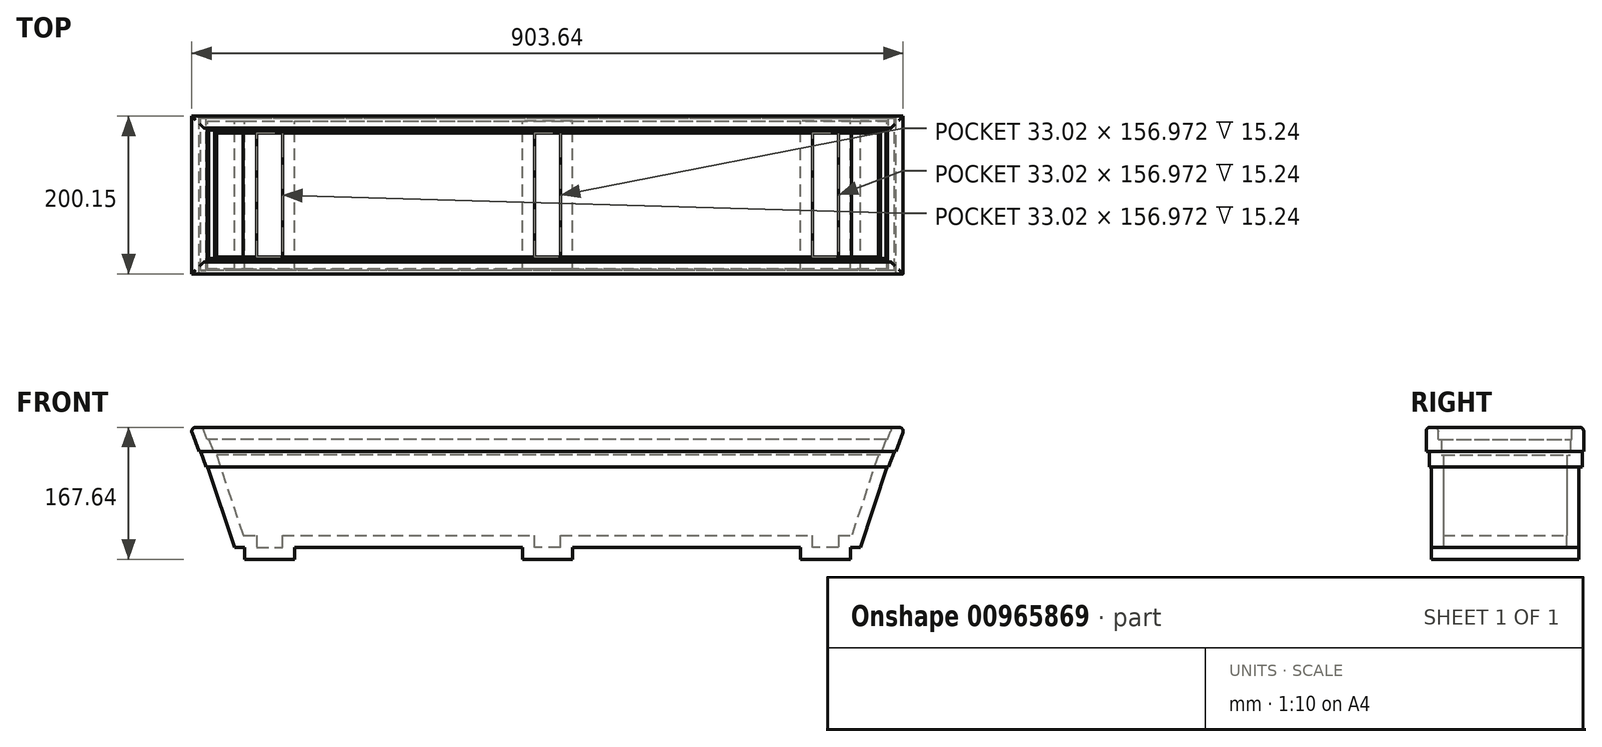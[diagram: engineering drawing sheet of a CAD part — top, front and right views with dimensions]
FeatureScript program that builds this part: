
annotation { "Feature Type Name" : "Feature", "Feature Type Description" : "" }
export const myFeature = defineFeature(function(context is Context, id is Id, definition is map)
    precondition{}
    {
        {
            var Q0;
            Q0=qCreatedBy(makeId("Front.planeOp"),FACE);
            var sketch = newSketch(context, id + "F0", { "sketchPlane" : qUnion([Q0])});
            skLineSegment(sketch, "E0", {"start": v(-96.9, 71.44) * mm, "end": v(811.15, 71.44) * mm});
            skLineSegment(sketch, "E1", {"start": v(-85.58, 40.7) * mm, "end": v(-83.56, 40.7) * mm});
            skLineSegment(sketch, "E2", {"start": v(-83.56, 40.7) * mm, "end": v(-76.36, 21.22) * mm});
            skLineSegment(sketch, "E3", {"start": v(-74.34, 21.22) * mm, "end": v(-40.27, -80.96) * mm});
            skLineSegment(sketch, "E4", {"start": v(-85.58, 40.7) * mm, "end": v(-96.9, 71.44) * mm});
            skLineSegment(sketch, "E5", {"start": v(-74.34, 21.22) * mm, "end": v(-76.36, 21.22) * mm});
            skLineSegment(sketch, "E6", {"start": v(-40.27, -80.96) * mm, "end": v(754.52, -80.96) * mm});
            skLineSegment(sketch, "E7.MirrorCS", {"start": v(799.83, 40.7) * mm, "end": v(797.8, 40.7) * mm});
            skLineSegment(sketch, "E8.MirrorCS", {"start": v(799.83, 40.7) * mm, "end": v(811.15, 71.44) * mm});
            skLineSegment(sketch, "E9.MirrorCS", {"start": v(788.58, 21.22) * mm, "end": v(790.6, 21.22) * mm});
            skLineSegment(sketch, "E10.MirrorCS", {"start": v(788.58, 21.22) * mm, "end": v(754.52, -80.96) * mm});
            skLineSegment(sketch, "E11.MirrorCS", {"start": v(797.8, 40.7) * mm, "end": v(790.6, 21.22) * mm});
            skLineSegment(sketch, "E12", {"start": v(10.53, -80.96) * mm, "end": v(357.12, -80.96) * mm});
            skLineSegment(sketch, "E13", {"start": v(754.52, -80.96) * mm, "end": v(741.82, -80.96) * mm});
            skLineSegment(sketch, "E14", {"start": v(741.82, -80.96) * mm, "end": v(741.82, -96.2) * mm});
            skLineSegment(sketch, "E15", {"start": v(741.82, -96.2) * mm, "end": v(678.32, -96.2) * mm});
            skLineSegment(sketch, "E16", {"start": v(678.32, -96.2) * mm, "end": v(678.32, -80.96) * mm});
            skLineSegment(sketch, "E17.MirrorCS", {"start": v(-27.57, -80.96) * mm, "end": v(-27.57, -96.2) * mm});
            skLineSegment(sketch, "E18.MirrorCS", {"start": v(-27.57, -96.2) * mm, "end": v(35.93, -96.2) * mm});
            skLineSegment(sketch, "E19.MirrorCS", {"start": v(35.93, -96.2) * mm, "end": v(35.93, -80.96) * mm});
            skLineSegment(sketch, "E20", {"start": v(357.12, -96.2) * mm, "end": v(325.37, -96.2) * mm});
            skLineSegment(sketch, "E21", {"start": v(325.37, -96.2) * mm, "end": v(388.87, -96.2) * mm});
            skLineSegment(sketch, "E22", {"start": v(325.37, -96.2) * mm, "end": v(325.37, -80.96) * mm});
            skLineSegment(sketch, "E23", {"start": v(388.87, -96.2) * mm, "end": v(388.87, -80.96) * mm});
            skSolve(sketch);
        }
        {
            var Q0;
            Q0 = qSketchRegion(id + "F0", true);
            extrude(context, id + "F1", {"entities" : qUnion([Q0]), "depth" : 187.45 * mm, "offsetDistance" : 25.4 * mm});
        }
        {
            var Q0;
            Q0=makeQuery(id+"F1.opExtrude","CAP_FACE",FACE,{"disambiguationData":[OSD([sQuery(id+"F0.wireOp",EDGE,"E0"),sQuery(id+"F0.wireOp",EDGE,"E1"),sQuery(id+"F0.wireOp",EDGE,"E2"),sQuery(id+"F0.wireOp",EDGE,"E3"),sQuery(id+"F0.wireOp",EDGE,"E4"),sQuery(id+"F0.wireOp",EDGE,"E5"),sQuery(id+"F0.wireOp",EDGE,"E6"),sQuery(id+"F0.wireOp",EDGE,"E7.MirrorCS"),sQuery(id+"F0.wireOp",EDGE,"E8.MirrorCS"),sQuery(id+"F0.wireOp",EDGE,"E9.MirrorCS"),sQuery(id+"F0.wireOp",EDGE,"E10.MirrorCS"),sQuery(id+"F0.wireOp",EDGE,"E11.MirrorCS"),sQuery(id+"F0.wireOp",EDGE,"E12"),sQuery(id+"F0.wireOp",EDGE,"E13"),sQuery(id+"F0.wireOp",EDGE,"E14"),sQuery(id+"F0.wireOp",EDGE,"E15"),sQuery(id+"F0.wireOp",EDGE,"E16"),sQuery(id+"F0.wireOp",EDGE,"E17.MirrorCS"),sQuery(id+"F0.wireOp",EDGE,"E18.MirrorCS"),sQuery(id+"F0.wireOp",EDGE,"E19.MirrorCS"),sQuery(id+"F0.wireOp",EDGE,"E21"),sQuery(id+"F0.wireOp",EDGE,"E22"),sQuery(id+"F0.wireOp",EDGE,"E23")])],"isStart":false});
            var sketch = newSketch(context, id + "F2", { "sketchPlane" : qUnion([Q0])});
            skLineSegment(sketch, "E24", {"start": v(-96.9, 71.44) * mm, "end": v(811.15, 71.44) * mm});
            skLineSegment(sketch, "E25", {"start": v(811.15, 71.44) * mm, "end": v(799.83, 40.7) * mm});
            skLineSegment(sketch, "E26", {"start": v(799.83, 40.7) * mm, "end": v(-85.58, 40.7) * mm});
            skLineSegment(sketch, "E27", {"start": v(-85.58, 40.7) * mm, "end": v(-96.9, 71.44) * mm});
            skSolve(sketch);
        }
        {
            var Q0;
            Q0 = qSketchRegion(id + "F2", true);
            extrude(context, id + "F3", {"entities" : qUnion([Q0]), "operationType" : NewBodyOperationType.ADD, "depth" : 6.35 * mm, "offsetDistance" : 25.4 * mm});
        }
        {
            var Q0;
            Q0=makeQuery(id+"F1.opExtrude","CAP_FACE",FACE,{"disambiguationData":[OSD([sQuery(id+"F0.wireOp",EDGE,"E0"),sQuery(id+"F0.wireOp",EDGE,"E1"),sQuery(id+"F0.wireOp",EDGE,"E2"),sQuery(id+"F0.wireOp",EDGE,"E3"),sQuery(id+"F0.wireOp",EDGE,"E4"),sQuery(id+"F0.wireOp",EDGE,"E5"),sQuery(id+"F0.wireOp",EDGE,"E6"),sQuery(id+"F0.wireOp",EDGE,"E7.MirrorCS"),sQuery(id+"F0.wireOp",EDGE,"E8.MirrorCS"),sQuery(id+"F0.wireOp",EDGE,"E9.MirrorCS"),sQuery(id+"F0.wireOp",EDGE,"E10.MirrorCS"),sQuery(id+"F0.wireOp",EDGE,"E11.MirrorCS"),sQuery(id+"F0.wireOp",EDGE,"E12"),sQuery(id+"F0.wireOp",EDGE,"E13"),sQuery(id+"F0.wireOp",EDGE,"E14"),sQuery(id+"F0.wireOp",EDGE,"E15"),sQuery(id+"F0.wireOp",EDGE,"E16"),sQuery(id+"F0.wireOp",EDGE,"E17.MirrorCS"),sQuery(id+"F0.wireOp",EDGE,"E18.MirrorCS"),sQuery(id+"F0.wireOp",EDGE,"E19.MirrorCS"),sQuery(id+"F0.wireOp",EDGE,"E21"),sQuery(id+"F0.wireOp",EDGE,"E22"),sQuery(id+"F0.wireOp",EDGE,"E23")])],"isStart":false});
            var sketch = newSketch(context, id + "F4", { "sketchPlane" : qUnion([Q0])});
            skLineSegment(sketch, "E28", {"start": v(797.8, 40.7) * mm, "end": v(790.6, 21.22) * mm});
            skLineSegment(sketch, "E29", {"start": v(790.6, 21.22) * mm, "end": v(-76.36, 21.22) * mm});
            skLineSegment(sketch, "E30", {"start": v(-76.36, 21.22) * mm, "end": v(-83.56, 40.7) * mm});
            skLineSegment(sketch, "E31", {"start": v(-83.56, 40.7) * mm, "end": v(797.8, 40.7) * mm});
            skSolve(sketch);
        }
        {
            var Q0;
            {var subQ4=sQuery(id+"F4.wireOp",EDGE,"E28");Q0=makeQuery(id+"F4.imprint","IMPRINT",FACE,{"disambiguationData":[TD([[makeQuery(id+"F4.imprint","IMPRINT",EDGE,{"derivedFrom":subQ4}),-1.0]])]});}
            extrude(context, id + "F5", {"entities" : qUnion([Q0]), "operationType" : NewBodyOperationType.ADD, "depth" : 2.03 * mm, "offsetDistance" : 25.4 * mm});
        }
        {
            var Q0;
            Q0=makeQuery(id+"F1.opExtrude","CAP_FACE",FACE,{"disambiguationData":[OSD([sQuery(id+"F0.wireOp",EDGE,"E0"),sQuery(id+"F0.wireOp",EDGE,"E1"),sQuery(id+"F0.wireOp",EDGE,"E2"),sQuery(id+"F0.wireOp",EDGE,"E3"),sQuery(id+"F0.wireOp",EDGE,"E4"),sQuery(id+"F0.wireOp",EDGE,"E5"),sQuery(id+"F0.wireOp",EDGE,"E6"),sQuery(id+"F0.wireOp",EDGE,"E7.MirrorCS"),sQuery(id+"F0.wireOp",EDGE,"E8.MirrorCS"),sQuery(id+"F0.wireOp",EDGE,"E9.MirrorCS"),sQuery(id+"F0.wireOp",EDGE,"E10.MirrorCS"),sQuery(id+"F0.wireOp",EDGE,"E11.MirrorCS"),sQuery(id+"F0.wireOp",EDGE,"E12"),sQuery(id+"F0.wireOp",EDGE,"E13"),sQuery(id+"F0.wireOp",EDGE,"E14"),sQuery(id+"F0.wireOp",EDGE,"E15"),sQuery(id+"F0.wireOp",EDGE,"E16"),sQuery(id+"F0.wireOp",EDGE,"E17.MirrorCS"),sQuery(id+"F0.wireOp",EDGE,"E18.MirrorCS"),sQuery(id+"F0.wireOp",EDGE,"E19.MirrorCS"),sQuery(id+"F0.wireOp",EDGE,"E21"),sQuery(id+"F0.wireOp",EDGE,"E22"),sQuery(id+"F0.wireOp",EDGE,"E23")])],"isStart":true});
            var sketch = newSketch(context, id + "F6", { "sketchPlane" : qUnion([Q0])});
            skLineSegment(sketch, "E32", {"start": v(-811.15, 71.44) * mm, "end": v(96.9, 71.44) * mm});
            skLineSegment(sketch, "E33", {"start": v(96.9, 71.44) * mm, "end": v(85.58, 40.7) * mm});
            skLineSegment(sketch, "E34", {"start": v(85.58, 40.7) * mm, "end": v(-797.8, 40.7) * mm});
            skLineSegment(sketch, "E35", {"start": v(-797.8, 40.7) * mm, "end": v(-799.83, 40.7) * mm});
            skLineSegment(sketch, "E36", {"start": v(-799.83, 40.7) * mm, "end": v(-811.15, 71.44) * mm});
            skSolve(sketch);
        }
        {
            var Q0;
            Q0 = qSketchRegion(id + "F6", true);
            extrude(context, id + "F7", {"entities" : qUnion([Q0]), "operationType" : NewBodyOperationType.ADD, "depth" : 6.35 * mm, "offsetDistance" : 25.4 * mm});
        }
        {
            var Q0;
            Q0=makeQuery(id+"F1.opExtrude","CAP_FACE",FACE,{"disambiguationData":[OSD([sQuery(id+"F0.wireOp",EDGE,"E0"),sQuery(id+"F0.wireOp",EDGE,"E1"),sQuery(id+"F0.wireOp",EDGE,"E2"),sQuery(id+"F0.wireOp",EDGE,"E3"),sQuery(id+"F0.wireOp",EDGE,"E4"),sQuery(id+"F0.wireOp",EDGE,"E5"),sQuery(id+"F0.wireOp",EDGE,"E6"),sQuery(id+"F0.wireOp",EDGE,"E7.MirrorCS"),sQuery(id+"F0.wireOp",EDGE,"E8.MirrorCS"),sQuery(id+"F0.wireOp",EDGE,"E9.MirrorCS"),sQuery(id+"F0.wireOp",EDGE,"E10.MirrorCS"),sQuery(id+"F0.wireOp",EDGE,"E11.MirrorCS"),sQuery(id+"F0.wireOp",EDGE,"E12"),sQuery(id+"F0.wireOp",EDGE,"E13"),sQuery(id+"F0.wireOp",EDGE,"E14"),sQuery(id+"F0.wireOp",EDGE,"E15"),sQuery(id+"F0.wireOp",EDGE,"E16"),sQuery(id+"F0.wireOp",EDGE,"E17.MirrorCS"),sQuery(id+"F0.wireOp",EDGE,"E18.MirrorCS"),sQuery(id+"F0.wireOp",EDGE,"E19.MirrorCS"),sQuery(id+"F0.wireOp",EDGE,"E21"),sQuery(id+"F0.wireOp",EDGE,"E22"),sQuery(id+"F0.wireOp",EDGE,"E23")])],"isStart":true});
            var sketch = newSketch(context, id + "F8", { "sketchPlane" : qUnion([Q0])});
            skLineSegment(sketch, "E37", {"start": v(-797.8, 40.7) * mm, "end": v(83.56, 40.7) * mm});
            skLineSegment(sketch, "E38", {"start": v(83.56, 40.7) * mm, "end": v(76.36, 21.22) * mm});
            skLineSegment(sketch, "E39", {"start": v(76.36, 21.22) * mm, "end": v(-790.6, 21.22) * mm});
            skLineSegment(sketch, "E40", {"start": v(-790.6, 21.22) * mm, "end": v(-797.8, 40.7) * mm});
            skSolve(sketch);
        }
        {
            var Q0;
            Q0=makeQuery(id+"F8.imprint","IMPRINT",FACE,{"disambiguationData":[TD([[makeQuery(id+"F8.imprint","IMPRINT",EDGE,{"derivedFrom":sQuery(id+"F8.wireOp",EDGE,"E37")}),1.0]])]});
            extrude(context, id + "F9", {"entities" : qUnion([Q0]), "operationType" : NewBodyOperationType.ADD, "depth" : 4.32 * mm, "offsetDistance" : 25.4 * mm});
        }
        {
            var Q0;
            Q0=makeQuery(id+"F7.boolean.opBoolean","MERGE",FACE,{"derivedFrom":[makeQuery(id+"F3.boolean.opBoolean","MERGE",FACE,{"derivedFrom":[makeQuery(id+"F1.opExtrude","SWEPT_FACE",FACE,{"disambiguationData":[OSD([sQuery(id+"F0.wireOp",EDGE,"E0")])]}),makeQuery(id+"F3.opExtrude","SWEPT_FACE",FACE,{"disambiguationData":[OSD([sQuery(id+"F2.wireOp",EDGE,"E24")])]})]}),makeQuery(id+"F7.opExtrude","SWEPT_FACE",FACE,{"disambiguationData":[OSD([sQuery(id+"F6.wireOp",EDGE,"E32")])]})]});
            shell(context, id + "F10", {"entities" : qUnion([Q0]), "thickness" : 15.24 * mm});
        }
        {
            var Q0;
            Q0=makeQuery(id+"F10.opShell","OFFSET_EDGE",EDGE,{"disambiguationData":[OSD([sQuery(id+"F2.wireOp",EDGE,"E24")])]});
            var Q1;
            Q1=makeQuery(id+"F10.opShell","OFFSET_EDGE",EDGE,{"disambiguationData":[OSD([sQuery(id+"F0.wireOp",EDGE,"E0"),sQuery(id+"F0.wireOp",EDGE,"E8.MirrorCS"),sQuery(id+"F2.wireOp",EDGE,"E24"),sQuery(id+"F2.wireOp",EDGE,"E25"),sQuery(id+"F6.wireOp",EDGE,"E32"),sQuery(id+"F6.wireOp",EDGE,"E36")])]});
            var Q2;
            Q2=makeQuery(id+"F10.opShell","OFFSET_EDGE",EDGE,{"disambiguationData":[OSD([sQuery(id+"F6.wireOp",EDGE,"E32")])]});
            var Q3;
            Q3=makeQuery(id+"F10.opShell","OFFSET_EDGE",EDGE,{"disambiguationData":[OSD([sQuery(id+"F0.wireOp",EDGE,"E0"),sQuery(id+"F0.wireOp",EDGE,"E4"),sQuery(id+"F2.wireOp",EDGE,"E24"),sQuery(id+"F2.wireOp",EDGE,"E27"),sQuery(id+"F6.wireOp",EDGE,"E32"),sQuery(id+"F6.wireOp",EDGE,"E33")])]});
            var Q4;
            Q4=makeQuery(id+"F7.boolean.opBoolean","MERGE",EDGE,{"derivedFrom":[makeQuery(id+"F3.boolean.opBoolean","MERGE",EDGE,{"derivedFrom":[makeQuery(id+"F1.opExtrude","SWEPT_EDGE",EDGE,{"disambiguationData":[OSD([sQuery(id+"F0.wireOp",EDGE,"E0"),sQuery(id+"F0.wireOp",EDGE,"E4")])]}),makeQuery(id+"F3.opExtrude","SWEPT_EDGE",EDGE,{"disambiguationData":[OSD([sQuery(id+"F2.wireOp",EDGE,"E24"),sQuery(id+"F2.wireOp",EDGE,"E27")])]})]}),makeQuery(id+"F7.opExtrude","SWEPT_EDGE",EDGE,{"disambiguationData":[OSD([sQuery(id+"F6.wireOp",EDGE,"E32"),sQuery(id+"F6.wireOp",EDGE,"E33")])]})]});
            var Q5;
            Q5=makeQuery(id+"F3.opExtrude","CAP_EDGE",EDGE,{"disambiguationData":[OSD([sQuery(id+"F2.wireOp",EDGE,"E24")])],"isStart":false});
            var Q6;
            Q6=makeQuery(id+"F7.opExtrude","CAP_EDGE",EDGE,{"disambiguationData":[OSD([sQuery(id+"F6.wireOp",EDGE,"E32")])],"isStart":false});
            var Q7;
            Q7=makeQuery(id+"F7.boolean.opBoolean","MERGE",EDGE,{"derivedFrom":[makeQuery(id+"F3.boolean.opBoolean","MERGE",EDGE,{"derivedFrom":[makeQuery(id+"F1.opExtrude","SWEPT_EDGE",EDGE,{"disambiguationData":[OSD([sQuery(id+"F0.wireOp",EDGE,"E0"),sQuery(id+"F0.wireOp",EDGE,"E8.MirrorCS")])]}),makeQuery(id+"F3.opExtrude","SWEPT_EDGE",EDGE,{"disambiguationData":[OSD([sQuery(id+"F2.wireOp",EDGE,"E24"),sQuery(id+"F2.wireOp",EDGE,"E25")])]})]}),makeQuery(id+"F7.opExtrude","SWEPT_EDGE",EDGE,{"disambiguationData":[OSD([sQuery(id+"F6.wireOp",EDGE,"E32"),sQuery(id+"F6.wireOp",EDGE,"E36")])]})]});
            fillet(context, id + "F11", {"entities" : qUnion([Q0, Q1, Q2, Q3, Q4, Q5, Q6, Q7]), "radius" : 5.08 * mm, "tangentPropagation" : true, "allowEdgeOverflow" : false});
        }
    });
